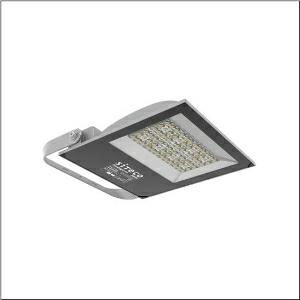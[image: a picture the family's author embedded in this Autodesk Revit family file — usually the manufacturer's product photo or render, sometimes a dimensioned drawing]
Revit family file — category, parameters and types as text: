
# Revit family: floodlight_fl_41_midi___pl32_5xa8581b1121_55a4
name_source: partatom
category: Lighting Fixtures
units: mm (PartAtom-declared; Revit-internal decimal feet)

## family parameters
Cut with Voids When Loaded = No
Host = Face
Light Source = No
Part Type = Normal
Room Calculation Point = No
Round Connector Dimension = Use Diameter
Shared = No

## types (1)
- --- (1 x LED, 26000 lm, 200 W, 3000K)
    Apparent Load = 200 VA
    CIE Flux Codes = 38 75 98 100 100
    Color Rendering = 70
    Color Temperature = 3000K
    Default Elevation = 1800 mm
    Description = Floodlight FL 41 midi, floodlight, primary light control with lens, of PMMA, primary optical cover: protective disc, transparent, light distribution: PL32, light emission: direct distribution, installation type: surface-mounted, LED, High Power LED, rated luminous flux: 26.000lm, luminous efficacy: 130lm/W, light colour: 730, colour temperature: 3000K, control gear: ON/OFF Multilumen, with cable, 3x 1.5mm², mains connection: 220..240V, AC, 50/60Hz, connection cable pre-assembled, cable length: 2m, rated input power: 200W, luminaire housing, of diecast aluminium, powder-coated, metallic grey (RAL 9006), length: 375mm, width: 335mm, height: 65mm, protection rating (complete): IP65, insulation class (complete): insulation class I (protective earthing), certification: CE, ENEC, impact resistance: IK08, permissible operating ambient temperature: -40..+40°C, permissible storage temperature: -40..+60°C, packaging unit: 1 piece

Light Distribution: PL32
    Height = 66 mm
    Lamp = 1 x LED
    Lamp Light Flux = 26000 lm
    Lamp Power = 200 W
    Lamp count = 1
    Length = 323 mm
    Luminous efficacy = 130 lm/W
    Manufacturer = Siteco
    ModVariant = No
    Model = 5XA8581B1121
    Mounting Place = Ceiling
    Mounting Type = Surface mounted
    Number of Poles = 1
    OnlyDefault = Yes
    Power Factor = 1
    Product Name = Floodlight FL 41 midi | PL32
    Product group = floodlight | ceiling mounted
    ProductGroupID = 305
    Protection Class = Protection class I
    Protection Degree = IP 65
    RLX_Detail_Level = 1
    RLX_Emergency_Light_Flux = 0 lm
    RLX_Emergency_Type = 0
    RLX_Emergency_Type_DB = No
    RlxData = <blob elided: 27413 chars, md5=9992b838>
    Socket = socket
    Standby Power = 0 W
    System Light Flux = 26000 lm
    System Power = 200 W
    Type Comments = factory setting: luminous flux: 100 % | (OFF | OFF | OFF)
    Type Image = l_1248229.jpg
    URL = http://relux.com
    VarID = @adj_131201
    Voltage = 0 V
    Weight = 0.00 kg
    Width = 331 mm

## geometry (parser evidence)
native form markers: Blend x4, Sweep x11
no freeform markers — native parametric forms only
